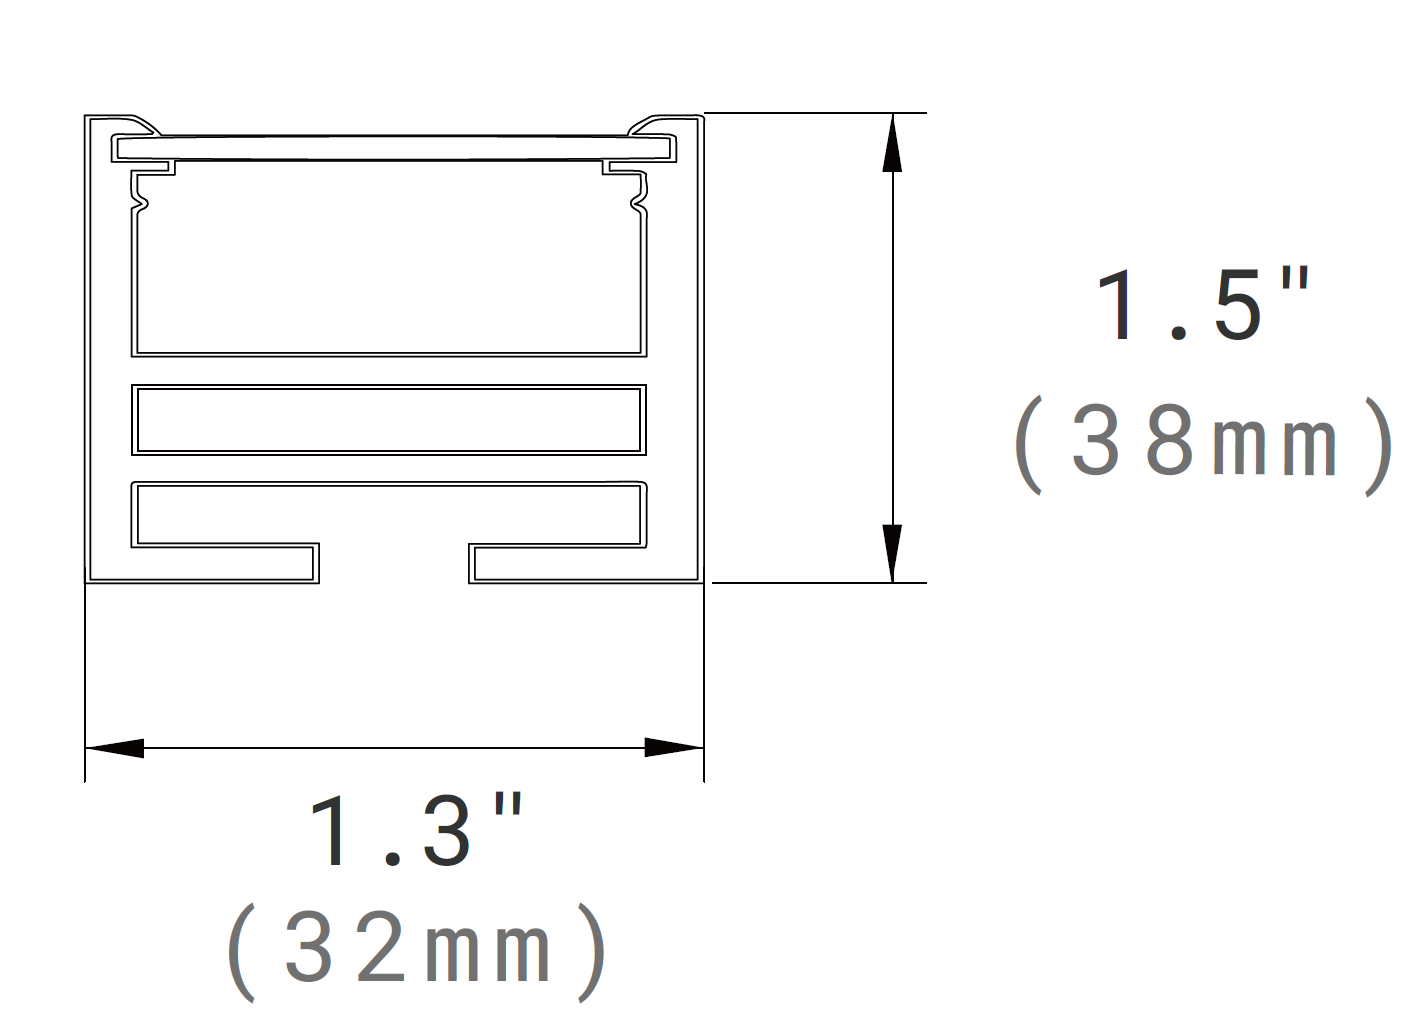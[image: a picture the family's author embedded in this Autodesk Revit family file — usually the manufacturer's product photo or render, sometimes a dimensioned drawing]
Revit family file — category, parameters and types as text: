
# Revit family: VRD-ACPMK
name_source: partatom
category: Lighting Fixtures
units: mm (PartAtom-declared; Revit-internal decimal feet)

## family parameters
Cut with Voids When Loaded = Yes
Host = Face
Light Source = Yes
Maintain Annotation Orientation = No
Part Type = Normal
Room Calculation Point = No
Round Connector Dimension = Use Diameter
Shared = No

## types (9) — shared parameters
Beam Angle = 0.00°
CRI = 90
Color Filter = 16777215
Default Elevation = 0' - 0"
Dimming Lamp Color Temperature Shift = <None>
Input Voltage = 120-277V
Lamp = LED
Load Classification = Lighting
Manufacturer = Above All Lighting
Note = The actual cable count varies with the fixture size.
Power Factor = 0.9
Suspension = 3' - 0"
Tilt Angle = 90.00°
URL = https://www.abovealllighting.com

## per-type parameters (varying)
| type | D1 | Model | Photometric Web File | R | Wattage Comments | cable |
| VRD-40W-4000K-ACPMK | 0' - 10" | VRD-4024-40901-ACPMK-WH | VRD-4024-40901 (1).IES | 0' - 11 13/16" | 40W | 0' - 11 25/32" |
| VRD-50W-3000K-ACPMK | 0' - 10" | VRD-5035-30901-ACPMK-WH | VRD_5035_30901.ies | 1' - 5 11/16" | 50W | 1' - 5 21/32" |
| VRD-80W-4000K-ACPMK | 0' - 10" | VRD-8047-40901-ACPMK-WH | VRD-8047-40901 (1).IES | 1' - 11 19/32" | 80W | 1' - 11 9/16" |
| VRD-100W-3000K-ACPMK | 0' - 10" | VRD-10059-30901-ACPMK-WH | VRD_10059_30901.ies | 2' - 5 9/16" | 100W | 2' - 5 17/32" |
| VRD-120W-3000K-ACPMK | 1' - 2" | VRD-12079-30901-ACPMK-WH | generic | 3' - 3 13/32" | 120W | 3' - 3 3/8" |
| VRD-160W-3000K-ACPMK | 1' - 2" | VRD-16098-30901-ACPMK-WH | generic | 4' - 1 3/16" | 160W | 4' - 1 5/32" |
| VRD-200W-3000K-ACPMK | 1' - 6" | VRD-200118-30901-ACPMK-WH | generic | 4' - 11 1/16" | 200W | 4' - 11 1/32" |
| VRD-300W-3000K-ACPMK | 1' - 8" | VRD-300158-30901-ACPMK-WH | generic | 6' - 7" | 300W | 6' - 6 31/32" |
| VRD-400W-3000K-ACPMK | 1' - 8" | VRD-400197-30901-ACPMK-WH | generic | 8' - 2 7/16" | 400W | 8' - 2 13/32" |

## geometry (parser evidence)
native form markers: Sweep x2
no freeform markers — native parametric forms only
